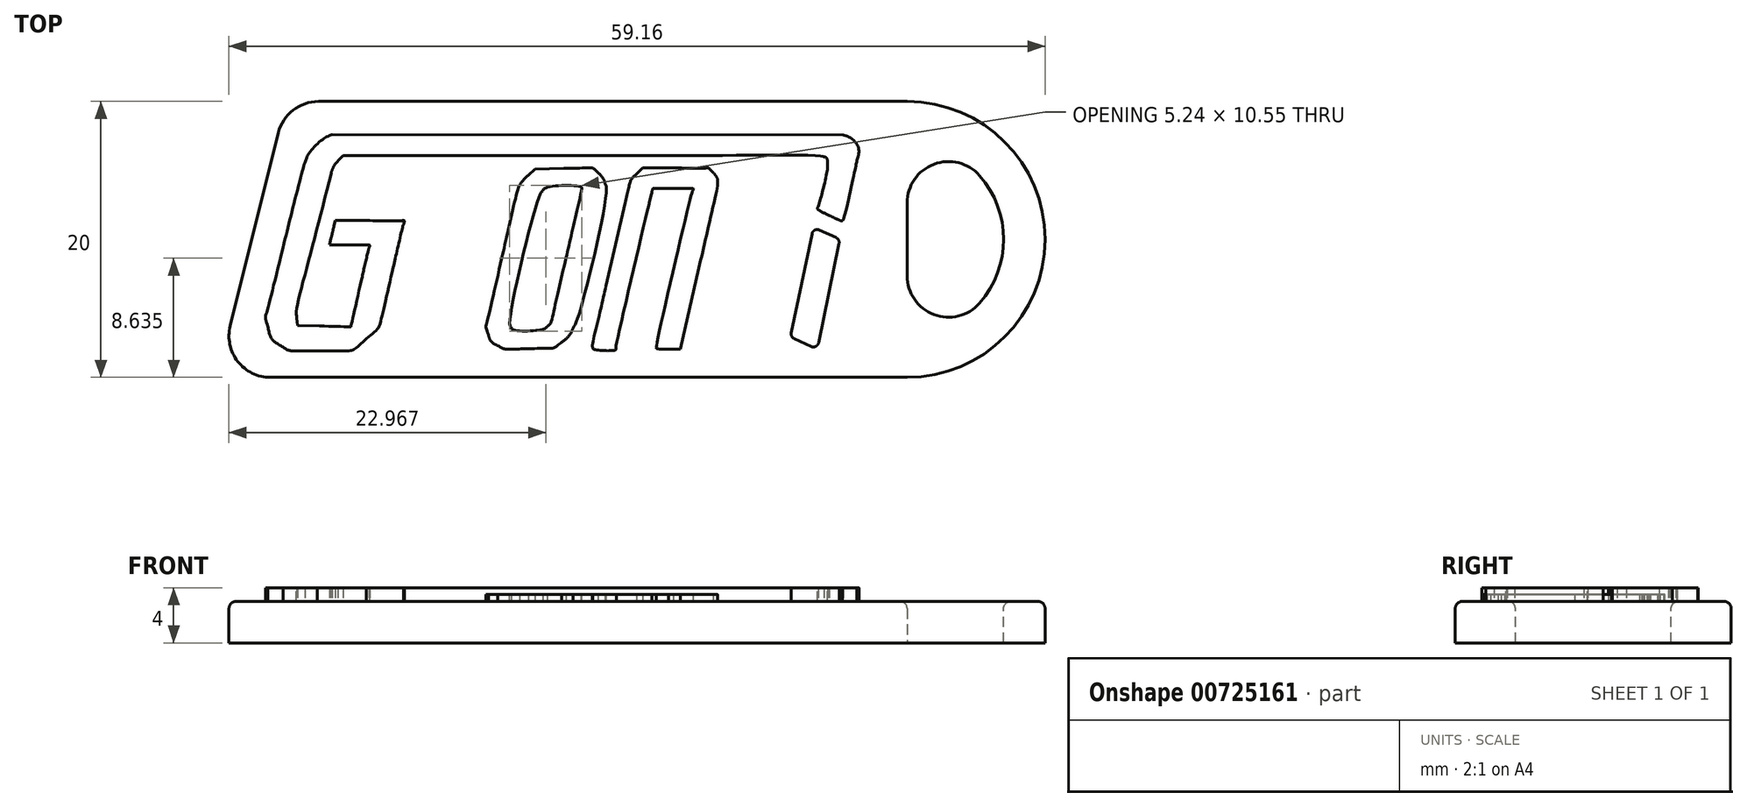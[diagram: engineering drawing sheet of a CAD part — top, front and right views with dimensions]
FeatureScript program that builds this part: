
annotation { "Feature Type Name" : "Feature", "Feature Type Description" : "" }
export const myFeature = defineFeature(function(context is Context, id is Id, definition is map)
    precondition{}
    {
        {
            var Q0;
            Q0=qCreatedBy(makeId("Top.planeOp"),FACE);
            var sketch = newSketch(context, id + "F0", { "sketchPlane" : qUnion([Q0])});
            skLineSegment(sketch, "E0.bottom", {"start": v(-20.01, 10) * mm, "end": v(25, 10) * mm});
            skLineSegment(sketch, "E0.top", {"start": v(-25, -10) * mm, "end": v(25, -10) * mm});
            skLineSegment(sketch, "E0.left", {"start": v(-25, 10) * mm, "end": v(-25, -10) * mm, "construction": true});
            skLineSegment(sketch, "E1", {"start": v(-25, -10) * mm, "end": v(-20.01, 10) * mm});
            skArc(sketch, "E2", {"start": v(25, -10) * mm, "mid": v(35, 0) * mm, "end": v(25, 10) * mm});
            skLineSegment(sketch, "E3", {"start": v(25, 0) * mm, "end": v(25, 7) * mm});
            skLineSegment(sketch, "E4", {"start": v(25, 0) * mm, "end": v(25, -7) * mm});
            skArc(sketch, "E5", {"start": v(25, -7) * mm, "mid": v(32, 0) * mm, "end": v(25, 7) * mm});
            skSolve(sketch);
        }
        {
            var Q0;
            Q0=makeQuery(id+"F0.imprint","IMPRINT",FACE,{"disambiguationData":[TD([[makeQuery(id+"F0.imprint","IMPRINT",EDGE,{"derivedFrom":sQuery(id+"F0.wireOp",EDGE,"E0.bottom")}),-1.0]])]});
            extrude(context, id + "F1", {"entities" : qUnion([Q0]), "oppositeDirection" : true, "depth" : 3 * mm, "offsetDistance" : 25 * mm});
        }
        {
            var Q0;
            Q0=qCreatedBy(makeId("Top.planeOp"),FACE);
            var sketch = newSketch(context, id + "F2", { "sketchPlane" : qUnion([Q0])});
            skFitSpline(sketch, "E6", {"points": [v(-20.23, -7.8) * mm, v(-20.88, -7.4) * mm, v(-21.15, -7.04) * mm, v(-21.34, -6.3) * mm]});
            skFitSpline(sketch, "E7", {"points": [v(-21.34, -6.3) * mm, v(-21.5, -5.68) * mm, v(-21.44, -5.34) * mm, v(-20.17, -0.26) * mm]});
            skFitSpline(sketch, "E8", {"points": [v(-20.17, -0.26) * mm, v(-19.42, 2.7) * mm, v(-18.74, 5.32) * mm, v(-18.64, 5.56) * mm]});
            skFitSpline(sketch, "E9", {"points": [v(-18.64, 5.56) * mm, v(-18.4, 6.18) * mm, v(-17.4, 7.23) * mm, v(-16.7, 7.6) * mm]});
            skFitSpline(sketch, "E10", {"points": [v(20.38, 7.58) * mm, v(21.12, 7.19) * mm, v(21.5, 6.46) * mm, v(21.36, 5.73) * mm]});
            skFitSpline(sketch, "E11", {"points": [v(21.36, 5.73) * mm, v(21.17, 4.77) * mm, v(20.36, 1.43) * mm, v(20.3, 1.37) * mm]});
            skFitSpline(sketch, "E12", {"points": [v(20.3, 1.37) * mm, v(20.28, 1.34) * mm, v(19.85, 1.5) * mm, v(19.37, 1.73) * mm]});
            skFitSpline(sketch, "E13", {"points": [v(19.37, 1.73) * mm, v(18.74, 2.03) * mm, v(18.5, 2.22) * mm, v(18.55, 2.39) * mm]});
            skFitSpline(sketch, "E14", {"points": [v(18.55, 2.39) * mm, v(18.85, 3.43) * mm, v(19.22, 5.1) * mm, v(19.22, 5.46) * mm]});
            skFitSpline(sketch, "E15", {"points": [v(19.22, 5.46) * mm, v(19.22, 5.73) * mm, v(19.13, 5.94) * mm, v(18.99, 6) * mm]});
            skFitSpline(sketch, "E16", {"points": [v(18.99, 6) * mm, v(18.86, 6.04) * mm, v(10.96, 6.08) * mm, v(1.43, 6.08) * mm]});
            skLineSegment(sketch, "E17", {"start": v(20.38, 7.58) * mm, "end": v(-16.7, 7.6) * mm});
            skFitSpline(sketch, "E18", {"points": [v(-16.25, 5.7) * mm, v(-16.45, 5.48) * mm, v(-16.68, 5.06) * mm, v(-16.75, 4.77) * mm]});
            skFitSpline(sketch, "E19", {"points": [v(-16.75, 4.77) * mm, v(-18.5, -1.97) * mm, v(-19.28, -5.24) * mm, v(-19.24, -5.7) * mm]});
            skLineSegment(sketch, "E20", {"start": v(1.43, 6.08) * mm, "end": v(-15.9, 6.08) * mm});
            skLineSegment(sketch, "E21", {"start": v(-15.9, 6.08) * mm, "end": v(-16.25, 5.7) * mm});
            skFitSpline(sketch, "E22", {"points": [v(-17.59, -6.28) * mm, v(-15.33, -6.33) * mm, v(-15.33, -6.33) * mm, v(-14.55, -2.91) * mm]});
            skFitSpline(sketch, "E23", {"points": [v(-14.55, -2.91) * mm, v(-14.3, -1.82) * mm, v(-14.06, -0.8) * mm, v(-14.02, -0.67) * mm]});
            skFitSpline(sketch, "E24", {"points": [v(-14.02, -0.67) * mm, v(-13.95, -0.43) * mm, v(-14.08, -0.4) * mm, v(-15.41, -0.4) * mm]});
            skLineSegment(sketch, "E25", {"start": v(-19.24, -5.7) * mm, "end": v(-19.2, -6.23) * mm});
            skLineSegment(sketch, "E26", {"start": v(-19.2, -6.23) * mm, "end": v(-17.59, -6.28) * mm});
            skFitSpline(sketch, "E27", {"points": [v(-16.76, 0.07) * mm, v(-16.7, 0.34) * mm, v(-16.6, 0.73) * mm, v(-16.55, 0.96) * mm]});
            skLineSegment(sketch, "E28", {"start": v(-15.41, -0.4) * mm, "end": v(-16.89, -0.4) * mm});
            skLineSegment(sketch, "E29", {"start": v(-16.89, -0.4) * mm, "end": v(-16.76, 0.07) * mm});
            skFitSpline(sketch, "E30", {"points": [v(-13.95, 1.36) * mm, v(-11.62, 1.36) * mm, v(-11.44, 1.34) * mm, v(-11.51, 1.1) * mm]});
            skFitSpline(sketch, "E31", {"points": [v(-11.51, 1.1) * mm, v(-11.56, 0.96) * mm, v(-11.93, -0.6) * mm, v(-12.33, -2.36) * mm]});
            skFitSpline(sketch, "E32", {"points": [v(-12.33, -2.36) * mm, v(-13.14, -5.86) * mm, v(-13.37, -6.46) * mm, v(-14.2, -7.19) * mm]});
            skFitSpline(sketch, "E33", {"points": [v(-14.2, -7.19) * mm, v(-15.1, -7.97) * mm, v(-15.5, -8.08) * mm, v(-17.75, -8.08) * mm]});
            skFitSpline(sketch, "E34", {"points": [v(-17.75, -8.08) * mm, v(-19.47, -8.08) * mm, v(-19.85, -8.03) * mm, v(-20.23, -7.8) * mm]});
            skLineSegment(sketch, "E35", {"start": v(-16.55, 0.96) * mm, "end": v(-16.46, 1.36) * mm});
            skLineSegment(sketch, "E36", {"start": v(-16.46, 1.36) * mm, "end": v(-13.95, 1.36) * mm});
            skFitSpline(sketch, "E37", {"points": [v(-11.67, -7.94) * mm, v(-12.64, -7.52) * mm, v(-12.76, -6.7) * mm, v(-12.2, -4.35) * mm]});
            skFitSpline(sketch, "E38", {"points": [v(-10.98, -2.91) * mm, v(-10.22, -2.91) * mm, v(-10.12, -2.95) * mm, v(-10.18, -3.17) * mm]});
            skFitSpline(sketch, "E39", {"points": [v(-10.18, -3.17) * mm, v(-10.49, -4.28) * mm, v(-10.87, -6.23) * mm, v(-10.8, -6.4) * mm]});
            skFitSpline(sketch, "E40", {"points": [v(-10.8, -6.4) * mm, v(-10.68, -6.72) * mm, v(-8.9, -6.68) * mm, v(-8.62, -6.34) * mm]});
            skFitSpline(sketch, "E41", {"points": [v(-8.62, -6.34) * mm, v(-8.27, -5.94) * mm, v(-7.57, -2.64) * mm, v(-7.78, -2.38) * mm]});
            skFitSpline(sketch, "E42", {"points": [v(-7.78, -2.38) * mm, v(-7.87, -2.27) * mm, v(-8.48, -1.9) * mm, v(-9.13, -1.55) * mm]});
            skFitSpline(sketch, "E43", {"points": [v(-9.13, -1.55) * mm, v(-10.45, -0.85) * mm, v(-11.01, -0.29) * mm, v(-11.01, 0.33) * mm]});
            skFitSpline(sketch, "E44", {"points": [v(-11.01, 0.33) * mm, v(-11.01, 1.04) * mm, v(-10.4, 3.47) * mm, v(-10.1, 3.97) * mm]});
            skFitSpline(sketch, "E45", {"points": [v(-10.1, 3.97) * mm, v(-9.58, 4.84) * mm, v(-9.03, 5.05) * mm, v(-7.28, 5.05) * mm]});
            skFitSpline(sketch, "E46", {"points": [v(-7.28, 5.05) * mm, v(-5.84, 5.05) * mm, v(-5.7, 5.02) * mm, v(-5.29, 4.68) * mm]});
            skFitSpline(sketch, "E47", {"points": [v(-5.29, 4.68) * mm, v(-4.69, 4.18) * mm, v(-4.64, 3.73) * mm, v(-5.01, 2.06) * mm]});
            skLineSegment(sketch, "E48", {"start": v(-12.2, -4.35) * mm, "end": v(-11.86, -2.91) * mm});
            skLineSegment(sketch, "E49", {"start": v(-11.86, -2.91) * mm, "end": v(-10.98, -2.91) * mm});
            skFitSpline(sketch, "E50", {"points": [v(-6.18, 0.62) * mm, v(-6.76, 0.62) * mm, v(-7.03, 0.68) * mm, v(-7.03, 0.8) * mm]});
            skFitSpline(sketch, "E51", {"points": [v(-7.03, 0.8) * mm, v(-7.03, 0.91) * mm, v(-6.9, 1.54) * mm, v(-6.73, 2.22) * mm]});
            skFitSpline(sketch, "E52", {"points": [v(-6.73, 2.22) * mm, v(-6.57, 2.9) * mm, v(-6.44, 3.47) * mm, v(-6.44, 3.5) * mm]});
            skFitSpline(sketch, "E53", {"points": [v(-6.44, 3.5) * mm, v(-6.44, 3.55) * mm, v(-6.9, 3.57) * mm, v(-7.47, 3.57) * mm]});
            skFitSpline(sketch, "E54", {"points": [v(-7.47, 3.57) * mm, v(-8.67, 3.57) * mm, v(-8.64, 3.6) * mm, v(-9.01, 1.9) * mm]});
            skFitSpline(sketch, "E55", {"points": [v(-9.01, 1.9) * mm, v(-9.2, 1.07) * mm, v(-9.22, 0.7) * mm, v(-9.1, 0.56) * mm]});
            skFitSpline(sketch, "E56", {"points": [v(-9.1, 0.56) * mm, v(-9.02, 0.46) * mm, v(-8.34, 0.05) * mm, v(-7.6, -0.34) * mm]});
            skFitSpline(sketch, "E57", {"points": [v(-7.6, -0.34) * mm, v(-6.22, -1.07) * mm, v(-5.85, -1.48) * mm, v(-5.85, -2.26) * mm]});
            skFitSpline(sketch, "E58", {"points": [v(-5.85, -2.26) * mm, v(-5.85, -2.9) * mm, v(-6.72, -6.46) * mm, v(-7, -6.92) * mm]});
            skFitSpline(sketch, "E59", {"points": [v(-7, -6.92) * mm, v(-7.48, -7.75) * mm, v(-8.1, -8) * mm, v(-9.83, -8.04) * mm]});
            skFitSpline(sketch, "E60", {"points": [v(-9.83, -8.04) * mm, v(-10.68, -8.06) * mm, v(-11.51, -8.02) * mm, v(-11.67, -7.94) * mm]});
            skLineSegment(sketch, "E61", {"start": v(-5.01, 2.06) * mm, "end": v(-5.33, 0.62) * mm});
            skLineSegment(sketch, "E62", {"start": v(-5.33, 0.62) * mm, "end": v(-6.18, 0.62) * mm});
            skFitSpline(sketch, "E63", {"points": [v(-4.67, -7.83) * mm, v(-5.03, -7.64) * mm, v(-5.24, -7.4) * mm, v(-5.36, -7.02) * mm]});
            skFitSpline(sketch, "E64", {"points": [v(-5.36, -7.02) * mm, v(-5.52, -6.53) * mm, v(-5.43, -6.02) * mm, v(-4.39, -1.49) * mm]});
            skFitSpline(sketch, "E65", {"points": [v(-4.39, -1.49) * mm, v(-3.76, 1.26) * mm, v(-3.17, 3.64) * mm, v(-3.08, 3.8) * mm]});
            skFitSpline(sketch, "E66", {"points": [v(-3.08, 3.8) * mm, v(-3, 3.96) * mm, v(-2.72, 4.29) * mm, v(-2.46, 4.53) * mm]});
            skFitSpline(sketch, "E67", {"points": [v(0.1, 5.02) * mm, v(2.16, 5.07) * mm, v(2.2, 5.06) * mm, v(2.6, 4.7) * mm]});
            skFitSpline(sketch, "E68", {"points": [v(2.6, 4.7) * mm, v(2.8, 4.5) * mm, v(3.03, 4.15) * mm, v(3.09, 3.93) * mm]});
            skFitSpline(sketch, "E69", {"points": [v(3.09, 3.93) * mm, v(3.2, 3.47) * mm, v(1.23, -5.48) * mm, v(0.78, -6.54) * mm]});
            skFitSpline(sketch, "E70", {"points": [v(0.78, -6.54) * mm, v(0.64, -6.88) * mm, v(0.28, -7.34) * mm, v(-0.03, -7.58) * mm]});
            skFitSpline(sketch, "E71", {"points": [v(-0.03, -7.58) * mm, v(-0.57, -7.98) * mm, v(-0.67, -8) * mm, v(-2.37, -8.05) * mm]});
            skFitSpline(sketch, "E72", {"points": [v(-2.37, -8.05) * mm, v(-3.86, -8.08) * mm, v(-4.24, -8.05) * mm, v(-4.67, -7.83) * mm]});
            skLineSegment(sketch, "E73", {"start": v(-2.46, 4.53) * mm, "end": v(-2, 4.98) * mm});
            skLineSegment(sketch, "E74", {"start": v(-2, 4.98) * mm, "end": v(0.1, 5.02) * mm});
            skFitSpline(sketch, "E75", {"points": [v(-1.08, -6.41) * mm, v(-0.9, -6.28) * mm, v(-0.52, -4.9) * mm, v(0.28, -1.46) * mm]});
            skFitSpline(sketch, "E76", {"points": [v(0.28, -1.46) * mm, v(0.88, 1.16) * mm, v(1.38, 3.36) * mm, v(1.38, 3.44) * mm]});
            skFitSpline(sketch, "E77", {"points": [v(1.38, 3.44) * mm, v(1.38, 3.67) * mm, v(-1.22, 3.6) * mm, v(-1.4, 3.37) * mm]});
            skFitSpline(sketch, "E78", {"points": [v(-1.4, 3.37) * mm, v(-1.62, 3.12) * mm, v(-3.8, -6.3) * mm, v(-3.7, -6.47) * mm]});
            skFitSpline(sketch, "E79", {"points": [v(-3.7, -6.47) * mm, v(-3.57, -6.68) * mm, v(-1.37, -6.63) * mm, v(-1.08, -6.41) * mm]});
            skFitSpline(sketch, "E80", {"points": [v(2.22, -7.97) * mm, v(2.19, -7.9) * mm, v(2.61, -5.9) * mm, v(3.17, -3.5) * mm]});
            skFitSpline(sketch, "E81", {"points": [v(3.17, -3.5) * mm, v(3.72, -1.11) * mm, v(4.35, 1.6) * mm, v(4.56, 2.5) * mm]});
            skFitSpline(sketch, "E82", {"points": [v(4.56, 2.5) * mm, v(4.88, 3.87) * mm, v(5.03, 4.25) * mm, v(5.39, 4.61) * mm]});
            skFitSpline(sketch, "E83", {"points": [v(8.22, 5.05) * mm, v(10.53, 5.05) * mm, v(10.63, 5.04) * mm, v(10.94, 4.7) * mm]});
            skFitSpline(sketch, "E84", {"points": [v(10.94, 4.7) * mm, v(11.11, 4.52) * mm, v(11.26, 4.2) * mm, v(11.26, 4) * mm]});
            skFitSpline(sketch, "E85", {"points": [v(11.26, 4) * mm, v(11.26, 3.8) * mm, v(10.65, 1) * mm, v(9.9, -2.21) * mm]});
            skLineSegment(sketch, "E86", {"start": v(5.39, 4.61) * mm, "end": v(5.82, 5.05) * mm});
            skLineSegment(sketch, "E87", {"start": v(5.82, 5.05) * mm, "end": v(8.22, 5.05) * mm});
            skFitSpline(sketch, "E88", {"points": [v(7.7, -8.08) * mm, v(7.22, -8.08) * mm, v(6.83, -8.02) * mm, v(6.83, -7.96) * mm]});
            skFitSpline(sketch, "E89", {"points": [v(6.83, -7.96) * mm, v(6.83, -7.83) * mm, v(9.3, 2.92) * mm, v(9.43, 3.32) * mm]});
            skFitSpline(sketch, "E90", {"points": [v(9.43, 3.32) * mm, v(9.5, 3.55) * mm, v(9.37, 3.57) * mm, v(8.04, 3.57) * mm]});
            skFitSpline(sketch, "E91", {"points": [v(8.04, 3.57) * mm, v(6.64, 3.57) * mm, v(6.57, 3.56) * mm, v(6.49, 3.24) * mm]});
            skFitSpline(sketch, "E92", {"points": [v(6.49, 3.24) * mm, v(6.3, 2.47) * mm, v(3.88, -7.94) * mm, v(3.88, -8) * mm]});
            skFitSpline(sketch, "E93", {"points": [v(3.88, -8) * mm, v(3.88, -8.12) * mm, v(2.28, -8.08) * mm, v(2.22, -7.97) * mm]});
            skLineSegment(sketch, "E94", {"start": v(9.9, -2.21) * mm, "end": v(8.55, -8.08) * mm});
            skLineSegment(sketch, "E95", {"start": v(8.55, -8.08) * mm, "end": v(7.7, -8.08) * mm});
            skFitSpline(sketch, "E96", {"points": [v(11.04, -7.94) * mm, v(10.07, -7.52) * mm, v(9.95, -6.7) * mm, v(10.5, -4.35) * mm]});
            skFitSpline(sketch, "E97", {"points": [v(11.72, -2.91) * mm, v(12.2, -2.91) * mm, v(12.59, -2.94) * mm, v(12.59, -2.98) * mm]});
            skFitSpline(sketch, "E98", {"points": [v(12.59, -2.98) * mm, v(12.59, -3) * mm, v(12.42, -3.75) * mm, v(12.21, -4.62) * mm]});
            skFitSpline(sketch, "E99", {"points": [v(12.21, -4.62) * mm, v(12, -5.5) * mm, v(11.87, -6.3) * mm, v(11.91, -6.4) * mm]});
            skFitSpline(sketch, "E100", {"points": [v(11.91, -6.4) * mm, v(12.03, -6.72) * mm, v(13.8, -6.67) * mm, v(14.1, -6.34) * mm]});
            skFitSpline(sketch, "E101", {"points": [v(14.1, -6.34) * mm, v(14.22, -6.2) * mm, v(14.5, -5.3) * mm, v(14.72, -4.35) * mm]});
            skFitSpline(sketch, "E102", {"points": [v(14.72, -4.35) * mm, v(15.03, -2.97) * mm, v(15.08, -2.56) * mm, v(14.94, -2.4) * mm]});
            skFitSpline(sketch, "E103", {"points": [v(14.94, -2.4) * mm, v(14.84, -2.28) * mm, v(14.23, -1.9) * mm, v(13.58, -1.55) * mm]});
            skFitSpline(sketch, "E104", {"points": [v(13.58, -1.55) * mm, v(12.26, -0.85) * mm, v(11.7, -0.29) * mm, v(11.7, 0.33) * mm]});
            skFitSpline(sketch, "E105", {"points": [v(11.7, 0.33) * mm, v(11.7, 1.04) * mm, v(12.3, 3.47) * mm, v(12.6, 3.97) * mm]});
            skFitSpline(sketch, "E106", {"points": [v(12.6, 3.97) * mm, v(13.14, 4.85) * mm, v(13.67, 5.05) * mm, v(15.49, 5.05) * mm]});
            skFitSpline(sketch, "E107", {"points": [v(15.49, 5.05) * mm, v(17.06, 5.05) * mm, v(17.11, 5.04) * mm, v(17.48, 4.64) * mm]});
            skFitSpline(sketch, "E108", {"points": [v(17.48, 4.64) * mm, v(18.03, 4.05) * mm, v(18.06, 3.7) * mm, v(17.71, 2.08) * mm]});
            skLineSegment(sketch, "E109", {"start": v(10.5, -4.35) * mm, "end": v(10.85, -2.91) * mm});
            skLineSegment(sketch, "E110", {"start": v(10.85, -2.91) * mm, "end": v(11.72, -2.91) * mm});
            skFitSpline(sketch, "E111", {"points": [v(16.54, 0.62) * mm, v(15.95, 0.62) * mm, v(15.68, 0.68) * mm, v(15.68, 0.8) * mm]});
            skFitSpline(sketch, "E112", {"points": [v(15.68, 0.8) * mm, v(15.68, 0.91) * mm, v(15.82, 1.54) * mm, v(15.98, 2.22) * mm]});
            skFitSpline(sketch, "E113", {"points": [v(15.98, 2.22) * mm, v(16.14, 2.9) * mm, v(16.27, 3.47) * mm, v(16.27, 3.5) * mm]});
            skFitSpline(sketch, "E114", {"points": [v(16.27, 3.5) * mm, v(16.27, 3.55) * mm, v(15.8, 3.57) * mm, v(15.24, 3.57) * mm]});
            skFitSpline(sketch, "E115", {"points": [v(15.24, 3.57) * mm, v(14.04, 3.57) * mm, v(14.1, 3.64) * mm, v(13.68, 1.82) * mm]});
            skLineSegment(sketch, "E116", {"start": v(17.71, 2.08) * mm, "end": v(17.4, 0.62) * mm});
            skLineSegment(sketch, "E117", {"start": v(17.4, 0.62) * mm, "end": v(16.54, 0.62) * mm});
            skFitSpline(sketch, "E118", {"points": [v(13.78, 0.44) * mm, v(13.97, 0.28) * mm, v(14.65, -0.1) * mm, v(15.27, -0.42) * mm]});
            skFitSpline(sketch, "E119", {"points": [v(15.27, -0.42) * mm, v(16.46, -1.02) * mm, v(16.86, -1.48) * mm, v(16.86, -2.26) * mm]});
            skFitSpline(sketch, "E120", {"points": [v(16.86, -2.26) * mm, v(16.86, -2.9) * mm, v(16, -6.46) * mm, v(15.72, -6.92) * mm]});
            skFitSpline(sketch, "E121", {"points": [v(15.72, -6.92) * mm, v(15.23, -7.75) * mm, v(14.6, -8) * mm, v(12.88, -8.04) * mm]});
            skFitSpline(sketch, "E122", {"points": [v(12.88, -8.04) * mm, v(12.03, -8.06) * mm, v(11.2, -8.02) * mm, v(11.04, -7.94) * mm]});
            skLineSegment(sketch, "E123", {"start": v(13.68, 1.82) * mm, "end": v(13.43, 0.72) * mm});
            skLineSegment(sketch, "E124", {"start": v(13.43, 0.72) * mm, "end": v(13.78, 0.44) * mm});
            skLineSegment(sketch, "E125", {"start": v(18.1, 0.4) * mm, "end": v(16.6, -6.78) * mm});
            skLineSegment(sketch, "E126", {"start": v(20.07, -0.3) * mm, "end": v(18.58, -7.5) * mm});
            skLineSegment(sketch, "E127", {"start": v(18.64, 0.68) * mm, "end": v(19.85, 0.13) * mm});
            skLineSegment(sketch, "E128", {"start": v(16.82, -7.2) * mm, "end": v(18.04, -7.76) * mm});
            skPoint(sketch, "E129.visualSharp", {"position": v(20.13, 0) * mm});
            skArc(sketch, "E129.filletArc", {"start": v(20.07, -0.3) * mm, "mid": v(20.03, -0.05) * mm, "end": v(19.85, 0.13) * mm});
            skPoint(sketch, "E130.visualSharp", {"position": v(18.48, -7.97) * mm});
            skArc(sketch, "E130.filletArc", {"start": v(18.04, -7.76) * mm, "mid": v(18.37, -7.76) * mm, "end": v(18.58, -7.5) * mm});
            skPoint(sketch, "E131.visualSharp", {"position": v(16.54, -7.08) * mm});
            skArc(sketch, "E131.filletArc", {"start": v(16.6, -6.78) * mm, "mid": v(16.64, -7.03) * mm, "end": v(16.82, -7.2) * mm});
            skPoint(sketch, "E132.visualSharp", {"position": v(18.2, 0.88) * mm});
            skArc(sketch, "E132.filletArc", {"start": v(18.64, 0.68) * mm, "mid": v(18.3, 0.67) * mm, "end": v(18.1, 0.4) * mm});
            skSolve(sketch);
        }
        {
            var Q0;
            Q0=makeQuery(id+"F2.imprint","IMPRINT",FACE,{"disambiguationData":[TD([[makeQuery(id+"F2.imprint","IMPRINT",EDGE,{"derivedFrom":sQuery(id+"F2.wireOp",EDGE,"E6")}),-1.0]])]});
            var Q1;
            Q1=makeQuery(id+"F2.imprint","IMPRINT",FACE,{"disambiguationData":[TD([[makeQuery(id+"F2.imprint","IMPRINT",EDGE,{"derivedFrom":sQuery(id+"F2.wireOp",EDGE,"E125")}),1.0]])]});
            extrude(context, id + "F3", {"entities" : qUnion([Q0, Q1]), "depth" : 1 * mm, "offsetDistance" : 25 * mm});
        }
        {
            var Q0;
            Q0=qCreatedBy(makeId("Top.planeOp"),FACE);
            var sketch = newSketch(context, id + "F4", { "sketchPlane" : qUnion([Q0])});
            skFitSpline(sketch, "E133", {"points": [v(17.27, -7.68) * mm, v(16.38, -7.27) * mm, v(16.35, -7.25) * mm, v(16.54, -6.95) * mm]});
            skFitSpline(sketch, "E134", {"points": [v(16.54, -6.95) * mm, v(16.72, -6.68) * mm, v(18.47, -7.48) * mm, v(18.48, -7.84) * mm]});
            skFitSpline(sketch, "E135", {"points": [v(18.48, -7.84) * mm, v(18.49, -8.17) * mm, v(18.3, -8.15) * mm, v(17.27, -7.68) * mm]});
            skFitSpline(sketch, "E136", {"points": [v(-20.23, -7.68) * mm, v(-20.88, -7.27) * mm, v(-21.15, -6.91) * mm, v(-21.34, -6.18) * mm]});
            skFitSpline(sketch, "E137", {"points": [v(-21.34, -6.18) * mm, v(-21.5, -5.55) * mm, v(-21.44, -5.22) * mm, v(-20.17, -0.13) * mm]});
            skFitSpline(sketch, "E138", {"points": [v(-20.17, -0.13) * mm, v(-19.42, 2.83) * mm, v(-18.74, 5.45) * mm, v(-18.64, 5.7) * mm]});
            skFitSpline(sketch, "E139", {"points": [v(-18.64, 5.7) * mm, v(-18.4, 6.31) * mm, v(-17.4, 7.35) * mm, v(-16.7, 7.73) * mm]});
            skFitSpline(sketch, "E140", {"points": [v(20.38, 7.71) * mm, v(21.12, 7.31) * mm, v(21.5, 6.6) * mm, v(21.36, 5.86) * mm]});
            skFitSpline(sketch, "E141", {"points": [v(21.36, 5.86) * mm, v(21.17, 4.9) * mm, v(20.36, 1.56) * mm, v(20.3, 1.5) * mm]});
            skFitSpline(sketch, "E142", {"points": [v(20.3, 1.5) * mm, v(20.28, 1.46) * mm, v(19.85, 1.63) * mm, v(19.37, 1.86) * mm]});
            skFitSpline(sketch, "E143", {"points": [v(19.37, 1.86) * mm, v(18.74, 2.16) * mm, v(18.5, 2.35) * mm, v(18.55, 2.51) * mm]});
            skFitSpline(sketch, "E144", {"points": [v(18.55, 2.51) * mm, v(18.85, 3.55) * mm, v(19.22, 5.23) * mm, v(19.22, 5.59) * mm]});
            skFitSpline(sketch, "E145", {"points": [v(19.22, 5.59) * mm, v(19.22, 5.85) * mm, v(19.13, 6.06) * mm, v(18.99, 6.12) * mm]});
            skFitSpline(sketch, "E146", {"points": [v(18.99, 6.12) * mm, v(18.86, 6.17) * mm, v(10.96, 6.2) * mm, v(1.43, 6.2) * mm]});
            skLineSegment(sketch, "E147", {"start": v(-16.7, 7.73) * mm, "end": v(-16.1, 8.05) * mm});
            skLineSegment(sketch, "E148", {"start": v(-16.1, 8.05) * mm, "end": v(1.82, 8.05) * mm});
            skLineSegment(sketch, "E149", {"start": v(1.82, 8.05) * mm, "end": v(19.74, 8.05) * mm});
            skLineSegment(sketch, "E150", {"start": v(19.74, 8.05) * mm, "end": v(20.38, 7.71) * mm});
            skLineSegment(sketch, "E151", {"start": v(20.38, 7.71) * mm, "end": v(-16.7, 7.73) * mm});
            skFitSpline(sketch, "E152", {"points": [v(-16.25, 5.82) * mm, v(-16.45, 5.6) * mm, v(-16.68, 5.19) * mm, v(-16.75, 4.9) * mm]});
            skFitSpline(sketch, "E153", {"points": [v(-16.75, 4.9) * mm, v(-18.5, -1.84) * mm, v(-19.28, -5.11) * mm, v(-19.24, -5.56) * mm]});
            skLineSegment(sketch, "E154", {"start": v(1.43, 6.2) * mm, "end": v(-15.9, 6.2) * mm});
            skLineSegment(sketch, "E155", {"start": v(-15.9, 6.2) * mm, "end": v(-16.25, 5.82) * mm});
            skLineSegment(sketch, "E156", {"start": v(-16.25, 5.82) * mm, "end": v(1.43, 6.2) * mm});
            skFitSpline(sketch, "E157", {"points": [v(-17.59, -6.15) * mm, v(-15.33, -6.2) * mm, v(-15.32, -6.2) * mm, v(-14.55, -2.79) * mm]});
            skFitSpline(sketch, "E158", {"points": [v(-14.55, -2.79) * mm, v(-14.3, -1.7) * mm, v(-14.06, -0.68) * mm, v(-14.02, -0.54) * mm]});
            skFitSpline(sketch, "E159", {"points": [v(-14.02, -0.54) * mm, v(-13.95, -0.3) * mm, v(-14.08, -0.28) * mm, v(-15.41, -0.28) * mm]});
            skLineSegment(sketch, "E160", {"start": v(-19.24, -5.56) * mm, "end": v(-19.2, -6.1) * mm});
            skLineSegment(sketch, "E161", {"start": v(-19.2, -6.1) * mm, "end": v(-17.59, -6.15) * mm});
            skLineSegment(sketch, "E162", {"start": v(-17.59, -6.15) * mm, "end": v(-19.24, -5.56) * mm});
            skFitSpline(sketch, "E163", {"points": [v(-16.76, 0.2) * mm, v(-16.7, 0.46) * mm, v(-16.6, 0.86) * mm, v(-16.55, 1.08) * mm]});
            skLineSegment(sketch, "E164", {"start": v(-15.41, -0.28) * mm, "end": v(-16.89, -0.28) * mm});
            skLineSegment(sketch, "E165", {"start": v(-16.89, -0.28) * mm, "end": v(-16.76, 0.2) * mm});
            skLineSegment(sketch, "E166", {"start": v(-16.76, 0.2) * mm, "end": v(-15.41, -0.28) * mm});
            skFitSpline(sketch, "E167", {"points": [v(-13.95, 1.49) * mm, v(-11.62, 1.49) * mm, v(-11.44, 1.47) * mm, v(-11.51, 1.23) * mm]});
            skFitSpline(sketch, "E168", {"points": [v(-11.51, 1.23) * mm, v(-11.56, 1.09) * mm, v(-11.93, -0.47) * mm, v(-12.33, -2.24) * mm]});
            skFitSpline(sketch, "E169", {"points": [v(-12.33, -2.24) * mm, v(-13.14, -5.73) * mm, v(-13.37, -6.33) * mm, v(-14.2, -7.06) * mm]});
            skFitSpline(sketch, "E170", {"points": [v(-14.2, -7.06) * mm, v(-15.1, -7.85) * mm, v(-15.5, -7.95) * mm, v(-17.75, -7.95) * mm]});
            skFitSpline(sketch, "E171", {"points": [v(-17.75, -7.95) * mm, v(-19.47, -7.95) * mm, v(-19.85, -7.9) * mm, v(-20.23, -7.68) * mm]});
            skLineSegment(sketch, "E172", {"start": v(-16.55, 1.08) * mm, "end": v(-16.46, 1.49) * mm});
            skLineSegment(sketch, "E173", {"start": v(-16.46, 1.49) * mm, "end": v(-13.95, 1.49) * mm});
            skLineSegment(sketch, "E174", {"start": v(-13.95, 1.49) * mm, "end": v(-16.55, 1.08) * mm});
            skFitSpline(sketch, "E175", {"points": [v(-11.67, -7.82) * mm, v(-12.64, -7.4) * mm, v(-12.76, -6.57) * mm, v(-12.2, -4.23) * mm]});
            skFitSpline(sketch, "E176", {"points": [v(-10.98, -2.79) * mm, v(-10.22, -2.79) * mm, v(-10.12, -2.82) * mm, v(-10.18, -3.05) * mm]});
            skFitSpline(sketch, "E177", {"points": [v(-10.18, -3.05) * mm, v(-10.49, -4.16) * mm, v(-10.87, -6.1) * mm, v(-10.8, -6.27) * mm]});
            skFitSpline(sketch, "E178", {"points": [v(-10.8, -6.27) * mm, v(-10.68, -6.6) * mm, v(-8.9, -6.55) * mm, v(-8.62, -6.22) * mm]});
            skFitSpline(sketch, "E179", {"points": [v(-8.62, -6.22) * mm, v(-8.27, -5.82) * mm, v(-7.57, -2.51) * mm, v(-7.78, -2.26) * mm]});
            skFitSpline(sketch, "E180", {"points": [v(-7.78, -2.26) * mm, v(-7.87, -2.15) * mm, v(-8.48, -1.77) * mm, v(-9.13, -1.43) * mm]});
            skFitSpline(sketch, "E181", {"points": [v(-9.13, -1.43) * mm, v(-10.45, -0.72) * mm, v(-11.01, -0.16) * mm, v(-11.01, 0.46) * mm]});
            skFitSpline(sketch, "E182", {"points": [v(-11.01, 0.46) * mm, v(-11.01, 1.17) * mm, v(-10.4, 3.6) * mm, v(-10.1, 4.1) * mm]});
            skFitSpline(sketch, "E183", {"points": [v(-10.1, 4.1) * mm, v(-9.57, 4.97) * mm, v(-9.03, 5.18) * mm, v(-7.28, 5.18) * mm]});
            skFitSpline(sketch, "E184", {"points": [v(-7.28, 5.18) * mm, v(-5.84, 5.18) * mm, v(-5.7, 5.15) * mm, v(-5.29, 4.8) * mm]});
            skFitSpline(sketch, "E185", {"points": [v(-5.29, 4.8) * mm, v(-4.69, 4.3) * mm, v(-4.64, 3.86) * mm, v(-5.01, 2.19) * mm]});
            skLineSegment(sketch, "E186", {"start": v(-12.2, -4.23) * mm, "end": v(-11.86, -2.79) * mm});
            skLineSegment(sketch, "E187", {"start": v(-11.86, -2.79) * mm, "end": v(-10.98, -2.79) * mm});
            skFitSpline(sketch, "E188", {"points": [v(-6.18, 0.75) * mm, v(-6.76, 0.75) * mm, v(-7.03, 0.8) * mm, v(-7.03, 0.94) * mm]});
            skFitSpline(sketch, "E189", {"points": [v(-7.03, 0.94) * mm, v(-7.03, 1.04) * mm, v(-6.9, 1.67) * mm, v(-6.73, 2.35) * mm]});
            skFitSpline(sketch, "E190", {"points": [v(-6.73, 2.35) * mm, v(-6.57, 3.02) * mm, v(-6.44, 3.6) * mm, v(-6.44, 3.64) * mm]});
            skFitSpline(sketch, "E191", {"points": [v(-6.44, 3.64) * mm, v(-6.44, 3.67) * mm, v(-6.9, 3.7) * mm, v(-7.47, 3.7) * mm]});
            skFitSpline(sketch, "E192", {"points": [v(-7.47, 3.7) * mm, v(-8.67, 3.7) * mm, v(-8.64, 3.73) * mm, v(-9.01, 2.03) * mm]});
            skFitSpline(sketch, "E193", {"points": [v(-9.01, 2.03) * mm, v(-9.2, 1.2) * mm, v(-9.22, 0.83) * mm, v(-9.1, 0.69) * mm]});
            skFitSpline(sketch, "E194", {"points": [v(-9.1, 0.69) * mm, v(-9.02, 0.58) * mm, v(-8.34, 0.18) * mm, v(-7.6, -0.21) * mm]});
            skFitSpline(sketch, "E195", {"points": [v(-7.6, -0.21) * mm, v(-6.22, -0.95) * mm, v(-5.85, -1.36) * mm, v(-5.85, -2.13) * mm]});
            skFitSpline(sketch, "E196", {"points": [v(-5.85, -2.13) * mm, v(-5.85, -2.78) * mm, v(-6.72, -6.33) * mm, v(-7, -6.8) * mm]});
            skFitSpline(sketch, "E197", {"points": [v(-7, -6.8) * mm, v(-7.48, -7.62) * mm, v(-8.1, -7.87) * mm, v(-9.83, -7.91) * mm]});
            skFitSpline(sketch, "E198", {"points": [v(-9.83, -7.91) * mm, v(-10.68, -7.93) * mm, v(-11.51, -7.89) * mm, v(-11.67, -7.82) * mm]});
            skLineSegment(sketch, "E199", {"start": v(-5.01, 2.19) * mm, "end": v(-5.33, 0.75) * mm});
            skLineSegment(sketch, "E200", {"start": v(-5.33, 0.75) * mm, "end": v(-6.18, 0.75) * mm});
            skFitSpline(sketch, "E201", {"points": [v(-4.67, -7.7) * mm, v(-5.03, -7.51) * mm, v(-5.24, -7.27) * mm, v(-5.36, -6.9) * mm]});
            skFitSpline(sketch, "E202", {"points": [v(-5.36, -6.9) * mm, v(-5.52, -6.4) * mm, v(-5.43, -5.9) * mm, v(-4.39, -1.36) * mm]});
            skFitSpline(sketch, "E203", {"points": [v(-4.39, -1.36) * mm, v(-3.76, 1.39) * mm, v(-3.17, 3.77) * mm, v(-3.08, 3.93) * mm]});
            skFitSpline(sketch, "E204", {"points": [v(-3.08, 3.93) * mm, v(-3, 4.09) * mm, v(-2.72, 4.42) * mm, v(-2.46, 4.66) * mm]});
            skFitSpline(sketch, "E205", {"points": [v(0.1, 5.15) * mm, v(2.16, 5.2) * mm, v(2.2, 5.19) * mm, v(2.6, 4.83) * mm]});
            skFitSpline(sketch, "E206", {"points": [v(2.6, 4.83) * mm, v(2.8, 4.63) * mm, v(3.03, 4.28) * mm, v(3.09, 4.05) * mm]});
            skFitSpline(sketch, "E207", {"points": [v(3.09, 4.05) * mm, v(3.2, 3.6) * mm, v(1.23, -5.35) * mm, v(0.78, -6.42) * mm]});
            skFitSpline(sketch, "E208", {"points": [v(0.78, -6.42) * mm, v(0.64, -6.75) * mm, v(0.28, -7.22) * mm, v(-0.03, -7.45) * mm]});
            skFitSpline(sketch, "E209", {"points": [v(-0.03, -7.45) * mm, v(-0.57, -7.86) * mm, v(-0.67, -7.88) * mm, v(-2.37, -7.92) * mm]});
            skFitSpline(sketch, "E210", {"points": [v(-2.37, -7.92) * mm, v(-3.86, -7.96) * mm, v(-4.24, -7.92) * mm, v(-4.67, -7.7) * mm]});
            skLineSegment(sketch, "E211", {"start": v(-2.46, 4.66) * mm, "end": v(-2, 5.1) * mm});
            skLineSegment(sketch, "E212", {"start": v(-2, 5.1) * mm, "end": v(0.1, 5.15) * mm});
            skFitSpline(sketch, "E213", {"points": [v(-1.08, -6.29) * mm, v(-0.9, -6.15) * mm, v(-0.52, -4.77) * mm, v(0.28, -1.34) * mm]});
            skFitSpline(sketch, "E214", {"points": [v(0.28, -1.34) * mm, v(0.88, 1.28) * mm, v(1.38, 3.49) * mm, v(1.38, 3.56) * mm]});
            skFitSpline(sketch, "E215", {"points": [v(1.38, 3.56) * mm, v(1.38, 3.8) * mm, v(-1.22, 3.73) * mm, v(-1.4, 3.5) * mm]});
            skFitSpline(sketch, "E216", {"points": [v(-1.4, 3.5) * mm, v(-1.62, 3.25) * mm, v(-3.8, -6.17) * mm, v(-3.7, -6.35) * mm]});
            skFitSpline(sketch, "E217", {"points": [v(-3.7, -6.35) * mm, v(-3.57, -6.55) * mm, v(-1.37, -6.5) * mm, v(-1.08, -6.29) * mm]});
            skFitSpline(sketch, "E218", {"points": [v(2.22, -7.84) * mm, v(2.19, -7.78) * mm, v(2.61, -5.77) * mm, v(3.17, -3.38) * mm]});
            skFitSpline(sketch, "E219", {"points": [v(3.17, -3.38) * mm, v(3.72, -0.99) * mm, v(4.35, 1.72) * mm, v(4.56, 2.64) * mm]});
            skFitSpline(sketch, "E220", {"points": [v(4.56, 2.64) * mm, v(4.88, 4) * mm, v(5.03, 4.38) * mm, v(5.39, 4.74) * mm]});
            skFitSpline(sketch, "E221", {"points": [v(8.22, 5.18) * mm, v(10.53, 5.18) * mm, v(10.63, 5.16) * mm, v(10.94, 4.83) * mm]});
            skFitSpline(sketch, "E222", {"points": [v(10.94, 4.83) * mm, v(11.11, 4.65) * mm, v(11.26, 4.33) * mm, v(11.26, 4.13) * mm]});
            skFitSpline(sketch, "E223", {"points": [v(11.26, 4.13) * mm, v(11.26, 3.94) * mm, v(10.65, 1.14) * mm, v(9.9, -2.09) * mm]});
            skLineSegment(sketch, "E224", {"start": v(5.39, 4.74) * mm, "end": v(5.82, 5.18) * mm});
            skLineSegment(sketch, "E225", {"start": v(5.82, 5.18) * mm, "end": v(8.22, 5.18) * mm});
            skFitSpline(sketch, "E226", {"points": [v(7.7, -7.95) * mm, v(7.22, -7.95) * mm, v(6.83, -7.9) * mm, v(6.83, -7.83) * mm]});
            skFitSpline(sketch, "E227", {"points": [v(6.83, -7.83) * mm, v(6.83, -7.7) * mm, v(9.3, 3.05) * mm, v(9.43, 3.44) * mm]});
            skFitSpline(sketch, "E228", {"points": [v(9.43, 3.44) * mm, v(9.5, 3.68) * mm, v(9.37, 3.7) * mm, v(8.04, 3.7) * mm]});
            skFitSpline(sketch, "E229", {"points": [v(8.04, 3.7) * mm, v(6.64, 3.7) * mm, v(6.57, 3.68) * mm, v(6.49, 3.37) * mm]});
            skFitSpline(sketch, "E230", {"points": [v(6.49, 3.37) * mm, v(6.3, 2.6) * mm, v(3.88, -7.82) * mm, v(3.88, -7.88) * mm]});
            skFitSpline(sketch, "E231", {"points": [v(3.88, -7.88) * mm, v(3.88, -8) * mm, v(2.28, -7.96) * mm, v(2.22, -7.84) * mm]});
            skLineSegment(sketch, "E232", {"start": v(9.9, -2.09) * mm, "end": v(8.55, -7.95) * mm});
            skLineSegment(sketch, "E233", {"start": v(8.55, -7.95) * mm, "end": v(7.7, -7.95) * mm});
            skFitSpline(sketch, "E234", {"points": [v(11.04, -7.82) * mm, v(10.07, -7.4) * mm, v(9.95, -6.57) * mm, v(10.5, -4.23) * mm]});
            skFitSpline(sketch, "E235", {"points": [v(11.72, -2.79) * mm, v(12.2, -2.79) * mm, v(12.59, -2.82) * mm, v(12.59, -2.85) * mm]});
            skFitSpline(sketch, "E236", {"points": [v(12.59, -2.85) * mm, v(12.59, -2.88) * mm, v(12.42, -3.62) * mm, v(12.21, -4.5) * mm]});
            skFitSpline(sketch, "E237", {"points": [v(12.21, -4.5) * mm, v(12, -5.37) * mm, v(11.87, -6.17) * mm, v(11.91, -6.28) * mm]});
            skFitSpline(sketch, "E238", {"points": [v(11.91, -6.28) * mm, v(12.03, -6.6) * mm, v(13.8, -6.54) * mm, v(14.1, -6.22) * mm]});
            skFitSpline(sketch, "E239", {"points": [v(14.1, -6.22) * mm, v(14.22, -6.08) * mm, v(14.5, -5.18) * mm, v(14.72, -4.22) * mm]});
            skFitSpline(sketch, "E240", {"points": [v(14.72, -4.22) * mm, v(15.03, -2.85) * mm, v(15.08, -2.44) * mm, v(14.94, -2.27) * mm]});
            skFitSpline(sketch, "E241", {"points": [v(14.94, -2.27) * mm, v(14.84, -2.15) * mm, v(14.23, -1.77) * mm, v(13.58, -1.43) * mm]});
            skFitSpline(sketch, "E242", {"points": [v(13.58, -1.43) * mm, v(12.26, -0.72) * mm, v(11.7, -0.16) * mm, v(11.7, 0.46) * mm]});
            skFitSpline(sketch, "E243", {"points": [v(11.7, 0.46) * mm, v(11.7, 1.17) * mm, v(12.3, 3.6) * mm, v(12.6, 4.1) * mm]});
            skFitSpline(sketch, "E244", {"points": [v(12.6, 4.1) * mm, v(13.14, 4.98) * mm, v(13.67, 5.18) * mm, v(15.49, 5.18) * mm]});
            skFitSpline(sketch, "E245", {"points": [v(15.49, 5.18) * mm, v(17.06, 5.18) * mm, v(17.11, 5.16) * mm, v(17.48, 4.77) * mm]});
            skFitSpline(sketch, "E246", {"points": [v(17.48, 4.77) * mm, v(18.03, 4.18) * mm, v(18.06, 3.82) * mm, v(17.71, 2.2) * mm]});
            skLineSegment(sketch, "E247", {"start": v(10.5, -4.23) * mm, "end": v(10.85, -2.79) * mm});
            skLineSegment(sketch, "E248", {"start": v(10.85, -2.79) * mm, "end": v(11.72, -2.79) * mm});
            skFitSpline(sketch, "E249", {"points": [v(16.54, 0.75) * mm, v(15.95, 0.75) * mm, v(15.68, 0.8) * mm, v(15.68, 0.94) * mm]});
            skFitSpline(sketch, "E250", {"points": [v(15.68, 0.94) * mm, v(15.68, 1.04) * mm, v(15.82, 1.67) * mm, v(15.98, 2.35) * mm]});
            skFitSpline(sketch, "E251", {"points": [v(15.98, 2.35) * mm, v(16.14, 3.02) * mm, v(16.27, 3.6) * mm, v(16.27, 3.64) * mm]});
            skFitSpline(sketch, "E252", {"points": [v(16.27, 3.64) * mm, v(16.27, 3.67) * mm, v(15.8, 3.7) * mm, v(15.24, 3.7) * mm]});
            skFitSpline(sketch, "E253", {"points": [v(15.24, 3.7) * mm, v(14.04, 3.7) * mm, v(14.1, 3.76) * mm, v(13.68, 1.94) * mm]});
            skLineSegment(sketch, "E254", {"start": v(17.71, 2.2) * mm, "end": v(17.4, 0.75) * mm});
            skLineSegment(sketch, "E255", {"start": v(17.4, 0.75) * mm, "end": v(16.54, 0.75) * mm});
            skFitSpline(sketch, "E256", {"points": [v(13.78, 0.56) * mm, v(13.97, 0.4) * mm, v(14.65, 0.02) * mm, v(15.27, -0.3) * mm]});
            skFitSpline(sketch, "E257", {"points": [v(15.27, -0.3) * mm, v(16.46, -0.9) * mm, v(16.86, -1.36) * mm, v(16.86, -2.13) * mm]});
            skFitSpline(sketch, "E258", {"points": [v(16.86, -2.13) * mm, v(16.86, -2.78) * mm, v(16, -6.33) * mm, v(15.72, -6.8) * mm]});
            skFitSpline(sketch, "E259", {"points": [v(15.72, -6.8) * mm, v(15.23, -7.62) * mm, v(14.6, -7.87) * mm, v(12.88, -7.91) * mm]});
            skFitSpline(sketch, "E260", {"points": [v(12.88, -7.91) * mm, v(12.03, -7.93) * mm, v(11.2, -7.89) * mm, v(11.04, -7.82) * mm]});
            skLineSegment(sketch, "E261", {"start": v(13.68, 1.94) * mm, "end": v(13.43, 0.85) * mm});
            skLineSegment(sketch, "E262", {"start": v(13.43, 0.85) * mm, "end": v(13.78, 0.56) * mm});
            skFitSpline(sketch, "E263", {"points": [v(17.76, -6.86) * mm, v(17.67, -6.75) * mm, v(17.4, -6.62) * mm, v(17.15, -6.57) * mm]});
            skFitSpline(sketch, "E264", {"points": [v(17.15, -6.57) * mm, v(16.84, -6.5) * mm, v(16.71, -6.4) * mm, v(16.71, -6.18) * mm]});
            skFitSpline(sketch, "E265", {"points": [v(16.71, -6.18) * mm, v(16.71, -5.93) * mm, v(16.78, -5.9) * mm, v(17.08, -5.97) * mm]});
            skFitSpline(sketch, "E266", {"points": [v(17.08, -5.97) * mm, v(17.36, -6.04) * mm, v(17.45, -6) * mm, v(17.45, -5.84) * mm]});
            skFitSpline(sketch, "E267", {"points": [v(17.45, -5.84) * mm, v(17.45, -5.72) * mm, v(17.49, -5.52) * mm, v(17.54, -5.4) * mm]});
            skFitSpline(sketch, "E268", {"points": [v(17.54, -5.4) * mm, v(17.59, -5.26) * mm, v(17.5, -5.14) * mm, v(17.31, -5.08) * mm]});
            skFitSpline(sketch, "E269", {"points": [v(17.31, -5.08) * mm, v(17.14, -5.02) * mm, v(17, -4.85) * mm, v(17, -4.7) * mm]});
            skFitSpline(sketch, "E270", {"points": [v(17, -4.7) * mm, v(17, -4.54) * mm, v(17.03, -4.41) * mm, v(17.06, -4.41) * mm]});
            skFitSpline(sketch, "E271", {"points": [v(17.06, -4.41) * mm, v(17.1, -4.41) * mm, v(17.56, -4.61) * mm, v(18.1, -4.86) * mm]});
            skFitSpline(sketch, "E272", {"points": [v(18.1, -4.86) * mm, v(18.86, -5.2) * mm, v(19.07, -5.36) * mm, v(19.02, -5.56) * mm]});
            skFitSpline(sketch, "E273", {"points": [v(19.02, -5.56) * mm, v(18.98, -5.7) * mm, v(18.87, -6.1) * mm, v(18.78, -6.44) * mm]});
            skFitSpline(sketch, "E274", {"points": [v(18.78, -6.44) * mm, v(18.65, -6.95) * mm, v(18.56, -7.07) * mm, v(18.28, -7.07) * mm]});
            skFitSpline(sketch, "E275", {"points": [v(18.28, -7.07) * mm, v(18.09, -7.07) * mm, v(17.85, -6.97) * mm, v(17.76, -6.86) * mm]});
            skFitSpline(sketch, "E276", {"points": [v(18.46, -6.04) * mm, v(18.5, -5.73) * mm, v(18.3, -5.45) * mm, v(18, -5.45) * mm]});
            skFitSpline(sketch, "E277", {"points": [v(18, -5.45) * mm, v(17.87, -5.44) * mm, v(17.86, -6.24) * mm, v(18, -6.38) * mm]});
            skFitSpline(sketch, "E278", {"points": [v(18, -6.38) * mm, v(18.18, -6.56) * mm, v(18.4, -6.39) * mm, v(18.46, -6.04) * mm]});
            skFitSpline(sketch, "E279", {"points": [v(18.74, -4.92) * mm, v(18.7, -4.87) * mm, v(18.73, -4.6) * mm, v(18.8, -4.3) * mm]});
            skFitSpline(sketch, "E280", {"points": [v(18.8, -4.3) * mm, v(18.92, -3.9) * mm, v(18.9, -3.75) * mm, v(18.75, -3.66) * mm]});
            skFitSpline(sketch, "E281", {"points": [v(18.75, -3.66) * mm, v(18.61, -3.57) * mm, v(18.52, -3.67) * mm, v(18.43, -4.05) * mm]});
            skFitSpline(sketch, "E282", {"points": [v(18.43, -4.05) * mm, v(18.25, -4.78) * mm, v(17.96, -4.61) * mm, v(18.02, -3.83) * mm]});
            skFitSpline(sketch, "E283", {"points": [v(18.02, -3.83) * mm, v(18.06, -3.35) * mm, v(18.02, -3.21) * mm, v(17.87, -3.26) * mm]});
            skFitSpline(sketch, "E284", {"points": [v(17.87, -3.26) * mm, v(17.76, -3.3) * mm, v(17.64, -3.52) * mm, v(17.6, -3.75) * mm]});
            skFitSpline(sketch, "E285", {"points": [v(17.6, -3.75) * mm, v(17.5, -4.27) * mm, v(17.16, -4.42) * mm, v(17.16, -3.94) * mm]});
            skFitSpline(sketch, "E286", {"points": [v(17.16, -3.94) * mm, v(17.16, -3.54) * mm, v(17.43, -2.5) * mm, v(17.54, -2.5) * mm]});
            skFitSpline(sketch, "E287", {"points": [v(17.54, -2.5) * mm, v(17.58, -2.5) * mm, v(18.01, -2.7) * mm, v(18.5, -2.95) * mm]});
            skFitSpline(sketch, "E288", {"points": [v(19.3, -3.94) * mm, v(19.12, -4.95) * mm, v(19, -5.17) * mm, v(18.74, -4.92) * mm]});
            skLineSegment(sketch, "E289", {"start": v(18.5, -2.95) * mm, "end": v(19.4, -3.4) * mm});
            skLineSegment(sketch, "E290", {"start": v(19.4, -3.4) * mm, "end": v(19.3, -3.94) * mm});
            skLineSegment(sketch, "E291", {"start": v(19.3, -3.94) * mm, "end": v(18.5, -2.95) * mm});
            skFitSpline(sketch, "E292", {"points": [v(19.23, -2.97) * mm, v(18.86, -2.32) * mm, v(18.81, -2.28) * mm, v(18.59, -2.47) * mm]});
            skFitSpline(sketch, "E293", {"points": [v(18.59, -2.47) * mm, v(18.42, -2.6) * mm, v(18.28, -2.61) * mm, v(17.98, -2.47) * mm]});
            skFitSpline(sketch, "E294", {"points": [v(17.98, -2.47) * mm, v(17.54, -2.27) * mm, v(17.42, -1.65) * mm, v(17.86, -1.83) * mm]});
            skFitSpline(sketch, "E295", {"points": [v(17.86, -1.83) * mm, v(18.33, -2) * mm, v(18.4, -1.98) * mm, v(18.46, -1.62) * mm]});
            skFitSpline(sketch, "E296", {"points": [v(18.46, -1.62) * mm, v(18.5, -1.38) * mm, v(18.4, -1.18) * mm, v(18.19, -1.02) * mm]});
            skFitSpline(sketch, "E297", {"points": [v(18.19, -1.02) * mm, v(18, -0.88) * mm, v(17.89, -0.66) * mm, v(17.92, -0.53) * mm]});
            skFitSpline(sketch, "E298", {"points": [v(17.92, -0.53) * mm, v(17.96, -0.32) * mm, v(18.1, -0.35) * mm, v(18.95, -0.74) * mm]});
            skFitSpline(sketch, "E299", {"points": [v(18.95, -0.74) * mm, v(19.73, -1.1) * mm, v(19.9, -1.25) * mm, v(19.85, -1.47) * mm]});
            skFitSpline(sketch, "E300", {"points": [v(19.85, -1.47) * mm, v(19.78, -1.73) * mm, v(19.75, -1.73) * mm, v(19.35, -1.53) * mm]});
            skFitSpline(sketch, "E301", {"points": [v(19.35, -1.53) * mm, v(18.83, -1.25) * mm, v(18.8, -1.44) * mm, v(19.28, -2.14) * mm]});
            skFitSpline(sketch, "E302", {"points": [v(19.28, -2.14) * mm, v(19.48, -2.44) * mm, v(19.6, -2.78) * mm, v(19.56, -2.95) * mm]});
            skFitSpline(sketch, "E303", {"points": [v(19.56, -2.95) * mm, v(19.46, -3.3) * mm, v(19.42, -3.3) * mm, v(19.23, -2.97) * mm]});
            skFitSpline(sketch, "E304", {"points": [v(18.74, -0.4) * mm, v(18.26, -0.2) * mm, v(18.04, 0) * mm, v(18.04, 0.18) * mm]});
            skFitSpline(sketch, "E305", {"points": [v(18.04, 0.18) * mm, v(18.04, 0.4) * mm, v(18.11, 0.44) * mm, v(18.41, 0.37) * mm]});
            skFitSpline(sketch, "E306", {"points": [v(18.41, 0.37) * mm, v(18.68, 0.3) * mm, v(18.78, 0.34) * mm, v(18.78, 0.5) * mm]});
            skFitSpline(sketch, "E307", {"points": [v(18.78, 0.5) * mm, v(18.78, 0.63) * mm, v(18.82, 0.83) * mm, v(18.86, 0.95) * mm]});
            skFitSpline(sketch, "E308", {"points": [v(18.86, 0.95) * mm, v(18.92, 1.09) * mm, v(18.84, 1.2) * mm, v(18.64, 1.26) * mm]});
            skFitSpline(sketch, "E309", {"points": [v(18.64, 1.26) * mm, v(18.47, 1.32) * mm, v(18.34, 1.49) * mm, v(18.34, 1.66) * mm]});
            skFitSpline(sketch, "E310", {"points": [v(18.34, 1.66) * mm, v(18.34, 2) * mm, v(18.63, 1.95) * mm, v(19.59, 1.43) * mm]});
            skFitSpline(sketch, "E311", {"points": [v(19.59, 1.43) * mm, v(20.1, 1.16) * mm, v(20.19, 1.03) * mm, v(20.22, 0.58) * mm]});
            skFitSpline(sketch, "E312", {"points": [v(20.22, 0.58) * mm, v(20.26, 0.13) * mm, v(20.32, 0.06) * mm, v(20.56, 0.12) * mm]});
            skFitSpline(sketch, "E313", {"points": [v(20.56, 0.12) * mm, v(20.77, 0.18) * mm, v(20.84, 0.12) * mm, v(20.84, -0.12) * mm]});
            skFitSpline(sketch, "E314", {"points": [v(20.84, -0.12) * mm, v(20.84, -0.45) * mm, v(20.49, -0.54) * mm, v(20.31, -0.26) * mm]});
            skFitSpline(sketch, "E315", {"points": [v(20.31, -0.26) * mm, v(20.24, -0.14) * mm, v(20.17, -0.2) * mm, v(20.09, -0.4) * mm]});
            skFitSpline(sketch, "E316", {"points": [v(20.09, -0.4) * mm, v(19.94, -0.8) * mm, v(19.64, -0.8) * mm, v(18.74, -0.4) * mm]});
            skLineSegment(sketch, "E317", {"start": v(19.23, -2.97) * mm, "end": v(19.23, -2.97) * mm});
            skFitSpline(sketch, "E318", {"points": [v(19.85, 0.23) * mm, v(19.92, 0.6) * mm, v(19.73, 0.9) * mm, v(19.43, 0.9) * mm]});
            skFitSpline(sketch, "E319", {"points": [v(19.43, 0.9) * mm, v(19.2, 0.9) * mm, v(19.07, 0.04) * mm, v(19.28, -0.05) * mm]});
            skFitSpline(sketch, "E320", {"points": [v(19.28, -0.05) * mm, v(19.63, -0.19) * mm, v(19.78, -0.12) * mm, v(19.85, 0.23) * mm]});
            skSolve(sketch);
        }
        {
            var Q0;
            Q0=makeQuery(id+"F4.imprint","IMPRINT",FACE,{"disambiguationData":[TD([[makeQuery(id+"F4.imprint","IMPRINT",EDGE,{"derivedFrom":sQuery(id+"F4.wireOp",EDGE,"E175")}),-1.0]])]});
            var Q1;
            Q1=makeQuery(id+"F4.imprint","IMPRINT",FACE,{"disambiguationData":[TD([[makeQuery(id+"F4.imprint","IMPRINT",EDGE,{"derivedFrom":sQuery(id+"F4.wireOp",EDGE,"E201")}),-1.0]])]});
            var Q2;
            Q2=makeQuery(id+"F4.imprint","IMPRINT",FACE,{"disambiguationData":[TD([[makeQuery(id+"F4.imprint","IMPRINT",EDGE,{"derivedFrom":sQuery(id+"F4.wireOp",EDGE,"E218")}),-1.0]])]});
            var Q3;
            Q3=makeQuery(id+"F4.imprint","IMPRINT",FACE,{"disambiguationData":[TD([[makeQuery(id+"F4.imprint","IMPRINT",EDGE,{"derivedFrom":sQuery(id+"F4.wireOp",EDGE,"E234")}),-1.0]])]});
            extrude(context, id + "F5", {"entities" : qUnion([Q0, Q1, Q2, Q3]), "depth" : 0.5 * mm, "offsetDistance" : 25 * mm});
        }
        {
            var Q0;
            Q0=makeQuery(id+"F1.opExtrude","SWEPT_EDGE",EDGE,{"disambiguationData":[OSD([sQuery(id+"F0.wireOp",EDGE,"E0.bottom"),sQuery(id+"F0.wireOp",EDGE,"E1")])]});
            var Q1;
            Q1=makeQuery(id+"F1.opExtrude","SWEPT_EDGE",EDGE,{"disambiguationData":[OSD([sQuery(id+"F0.wireOp",EDGE,"E0.top"),sQuery(id+"F0.wireOp",EDGE,"E1")])]});
            fillet(context, id + "F6", {"entities" : qUnion([Q0, Q1]), "radius" : 3 * mm, "tangentPropagation" : true, "allowEdgeOverflow" : false});
        }
        {
            var Q0;
            Q0=makeQuery(id+"F1.opExtrude","SWEPT_EDGE",EDGE,{"disambiguationData":[OSD([sQuery(id+"F0.wireOp",EDGE,"E3"),sQuery(id+"F0.wireOp",EDGE,"E5")])]});
            var Q1;
            Q1=makeQuery(id+"F1.opExtrude","SWEPT_EDGE",EDGE,{"disambiguationData":[OSD([sQuery(id+"F0.wireOp",EDGE,"E4"),sQuery(id+"F0.wireOp",EDGE,"E5")])]});
            fillet(context, id + "F7", {"entities" : qUnion([Q0, Q1]), "radius" : 3 * mm, "tangentPropagation" : true, "allowEdgeOverflow" : false});
        }
        {
            var Q0;
            Q0=makeQuery(id+"F1.opExtrude","CAP_FACE",FACE,{"disambiguationData":[OSD([sQuery(id+"F0.wireOp",EDGE,"E0.bottom"),sQuery(id+"F0.wireOp",EDGE,"E0.top"),sQuery(id+"F0.wireOp",EDGE,"E1"),sQuery(id+"F0.wireOp",EDGE,"E2"),sQuery(id+"F0.wireOp",EDGE,"E3"),sQuery(id+"F0.wireOp",EDGE,"E4"),sQuery(id+"F0.wireOp",EDGE,"E5")])],"isStart":true});
            fillet(context, id + "F8", {"entities" : qUnion([Q0]), "radius" : 0.5 * mm, "tangentPropagation" : true, "allowEdgeOverflow" : false});
        }
    });
